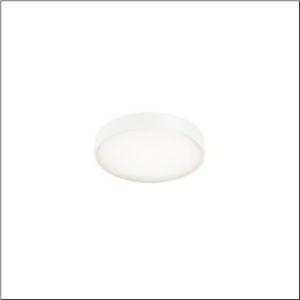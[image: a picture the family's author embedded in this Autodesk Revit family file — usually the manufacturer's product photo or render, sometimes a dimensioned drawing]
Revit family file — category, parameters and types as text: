
# Revit family: round_21_s_51mr34gd0321w
name_source: partatom
category: Lighting Fixtures
units: mm (PartAtom-declared; Revit-internal decimal feet)

## family parameters
Cut with Voids When Loaded = No
Host = Face
Light Source = No
Part Type = Normal
Room Calculation Point = No
Round Connector Dimension = Use Diameter
Shared = No

## types (1)
- Round 21 S (1 x LED, 3930 lm, 28.3 W, 3000K)
    Apparent Load = 28 VA
    CIE Flux Codes = 49 80 96 79 100
    Color Rendering = 80
    Color Temperature = 3000K
    Default Elevation = 1800 mm
    Description = Round 21 S, wall and ceiling luminaire, primary optical cover: cover, of PMMA, opal, light emission: direct/indirect distribution, primary light characteristic: symmetric, installation type: suspended mounting, surface-mounted, LED, rated luminous flux: 3.930lm, luminous efficacy: 139lm/W, light colour: 830, colour temperature: 3000K, control gear: DALI 2, with terminal, 5-pole, mains connection: 230V, AC, 50/60Hz, rated input power: 28.3W, housing, of aluminium, coated, white, diameter: 400mm, height: 62mm, protection rating (complete): IP40, insulation class (complete): insulation class I (protective earthing), certification: CE, impact resistance: IK04, permissible operating ambient temperature: -10..+35°C, packaging unit: 1 piece
    Height = 87 mm
    Lamp = 1 x LED
    Lamp Light Flux = 3930 lm
    Lamp Power = 28.3 W
    Lamp count = 1
    Length = 400 mm
    Luminous efficacy = 139 lm/W
    Manufacturer = Siteco
    ModVariant = No
    Model = 51MR34GD0321W
    Mounting Place = Ceiling
    Mounting Type = Surface mounted
    Number of Poles = 1
    OnlyDefault = Yes
    Power Factor = 1
    Product Name = Round 21 S
    Product group = wall and ceiling luminaire | ceiling mounted
    ProductGroupID = 304
    Protection Class = Protection class I
    Protection Degree = IP 40
    RLX_Detail_Level = 1
    RLX_Emergency_Light_Flux = 0 lm
    RLX_Emergency_Type = 0
    RLX_Emergency_Type_DB = No
    RlxData = <blob elided: 9937 chars, md5=104ea4ed>
    Socket = socket
    Standby Power = 0 W
    System Light Flux = 3930 lm
    System Power = 28 W
    Type Comments = Product without accessories
    Type Image = l_1258307.jpg
    URL = http://relux.com
    VarID = ---
    Voltage = 0 V
    Weight = 0.00 kg
    Width = 0 mm  [stored 0 ft]

note: [stored X ft] marks values corroborated as IEEE doubles in the binary element streams (Revit-internal decimal feet)

## geometry (parser evidence)
native form markers: Sweep x10
no freeform markers — native parametric forms only
